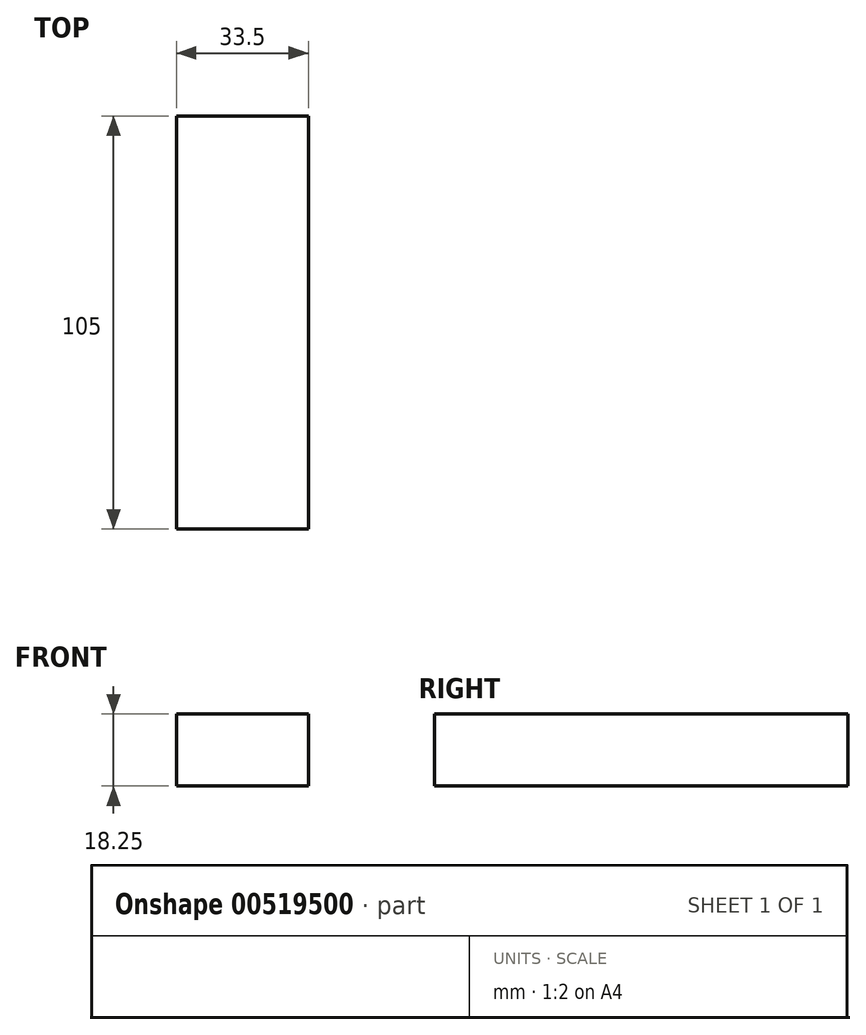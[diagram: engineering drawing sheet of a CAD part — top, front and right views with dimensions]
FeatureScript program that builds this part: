
annotation { "Feature Type Name" : "Feature", "Feature Type Description" : "" }
export const myFeature = defineFeature(function(context is Context, id is Id, definition is map)
    precondition{}
    {
        {
            var Q0;
            Q0=qCreatedBy(makeId("Top.planeOp"),FACE);
            var sketch = newSketch(context, id + "F0", { "sketchPlane" : qUnion([Q0])});
            skLineSegment(sketch, "E0.bottom", {"start": v(-16.75, 52.5) * mm, "end": v(16.75, 52.5) * mm});
            skLineSegment(sketch, "E0.top", {"start": v(-16.75, -52.5) * mm, "end": v(16.75, -52.5) * mm});
            skLineSegment(sketch, "E0.left", {"start": v(-16.75, 52.5) * mm, "end": v(-16.75, -52.5) * mm});
            skLineSegment(sketch, "E0.right", {"start": v(16.75, 52.5) * mm, "end": v(16.75, -52.5) * mm});
            skSolve(sketch);
        }
        {
            var Q0;
            Q0 = qSketchRegion(id + "F0", true);
            extrude(context, id + "F1", {"entities" : qUnion([Q0]), "depth" : 18.25 * mm, "offsetDistance" : 25 * mm});
        }
    });
